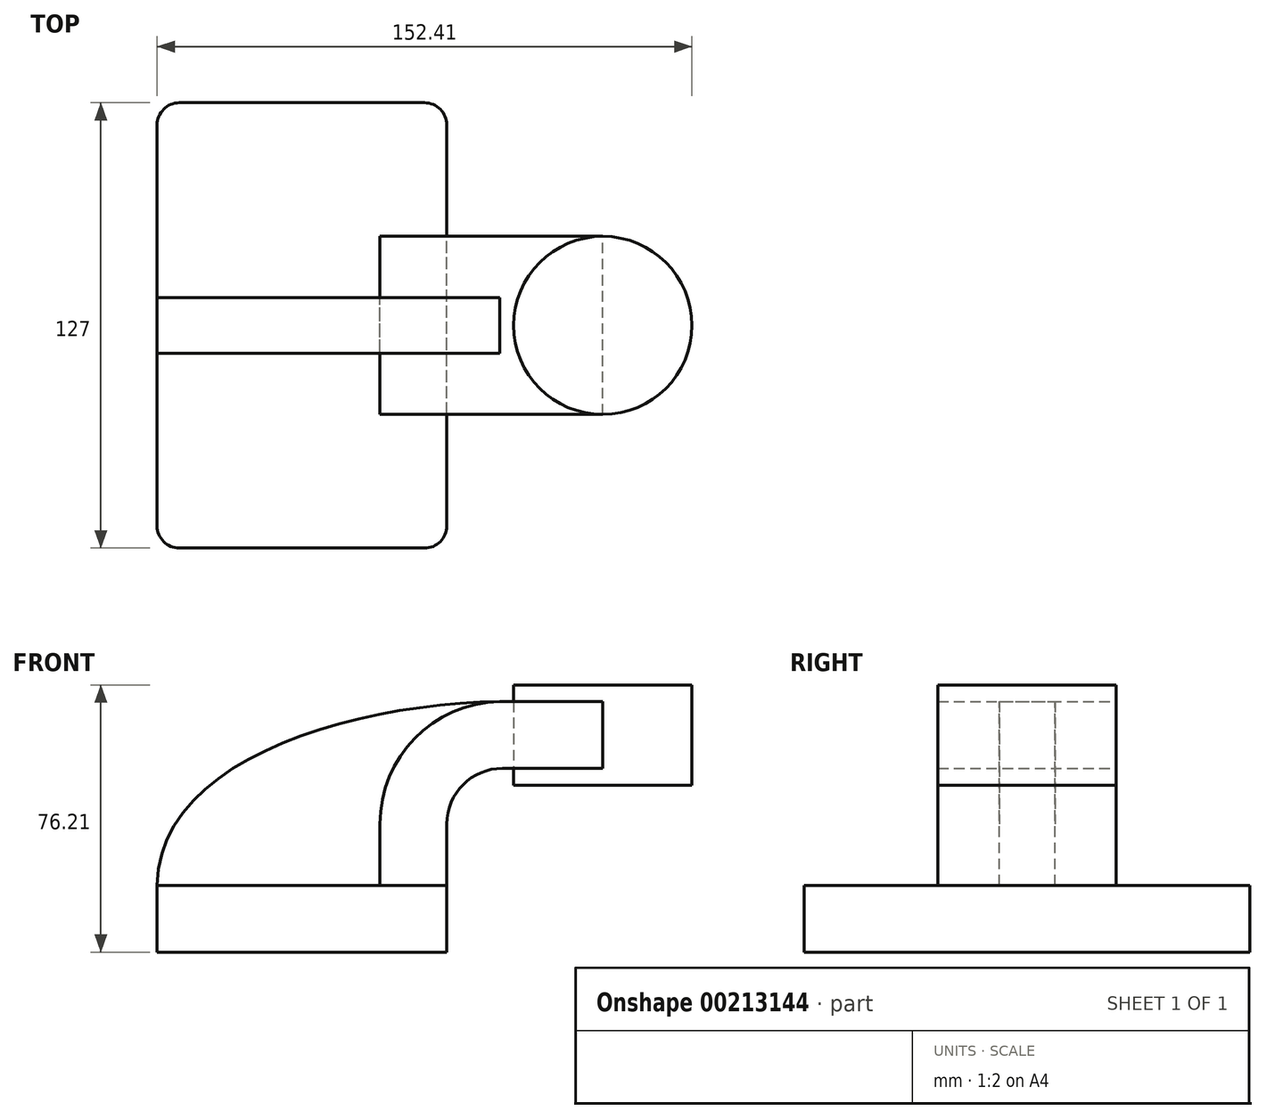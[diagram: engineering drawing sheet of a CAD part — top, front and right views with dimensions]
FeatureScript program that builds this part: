
annotation { "Feature Type Name" : "Feature", "Feature Type Description" : "" }
export const myFeature = defineFeature(function(context is Context, id is Id, definition is map)
    precondition{}
    {
        {
            var Q0;
            Q0=qCreatedBy(makeId("Front.planeOp"),FACE);
            var sketch = newSketch(context, id + "F0", { "sketchPlane" : qUnion([Q0])});
            skLineSegment(sketch, "E0.bottom", {"start": v(-41.28, 9.52) * mm, "end": v(41.28, 9.53) * mm});
            skLineSegment(sketch, "E0.top", {"start": v(-41.27, -9.52) * mm, "end": v(41.28, -9.52) * mm});
            skLineSegment(sketch, "E0.left", {"start": v(-41.28, 9.52) * mm, "end": v(-41.28, -9.53) * mm});
            skLineSegment(sketch, "E0.right", {"start": v(41.27, 9.53) * mm, "end": v(41.28, -9.52) * mm});
            skPoint(sketch, "E0.middle", {"position": v(0, 0) * mm});
            skLineSegment(sketch, "E1.bottom", {"start": v(111.12, 66.68) * mm, "end": v(60.32, 66.68) * mm});
            skLineSegment(sketch, "E1.top", {"start": v(111.12, 38.1) * mm, "end": v(60.32, 38.1) * mm});
            skLineSegment(sketch, "E1.left", {"start": v(111.12, 66.68) * mm, "end": v(111.12, 38.1) * mm});
            skLineSegment(sketch, "E1.right", {"start": v(60.32, 66.68) * mm, "end": v(60.32, 38.1) * mm});
            skPoint(sketch, "E1.middle", {"position": v(85.72, 52.39) * mm});
            skLineSegment(sketch, "E2", {"start": v(41.27, 9.53) * mm, "end": v(41.27, 27) * mm});
            skArc(sketch, "E3", {"start": v(41.27, 27) * mm, "mid": v(45.92, 38.23) * mm, "end": v(57.15, 42.88) * mm});
            skLineSegment(sketch, "E4", {"start": v(57.15, 42.88) * mm, "end": v(85.72, 42.88) * mm});
            skLineSegment(sketch, "E5.0", {"start": v(57.15, 61.93) * mm, "end": v(85.72, 61.93) * mm});
            skArc(sketch, "E5.1", {"start": v(22.22, 27) * mm, "mid": v(32.45, 51.7) * mm, "end": v(57.15, 61.93) * mm});
            skLineSegment(sketch, "E5.2", {"start": v(22.22, 9.53) * mm, "end": v(22.22, 27) * mm});
            skLineSegment(sketch, "E6", {"start": v(85.72, 38.1) * mm, "end": v(85.72, 66.68) * mm});
            skFitSpline(sketch, "E7", {"points": [v(-41.28, 9.52) * mm, v(57.15, 61.93) * mm], "startDerivative": vector(1.37, 108.93) * mm, "endDerivative": vector(126.16, 1.2) * mm});
            skSolve(sketch);
        }
        {
            var Q0;
            Q0=makeQuery(id+"F0.imprint","IMPRINT",FACE,{"disambiguationData":[TD([[makeQuery(id+"F0.imprint","IMPRINT",EDGE,{"derivedFrom":sQuery(id+"F0.wireOp",EDGE,"E0.top")}),1.0]])]});
            extrude(context, id + "F1", {"entities" : qUnion([Q0]), "endBound" : BoundingType.SYMMETRIC, "depth" : 127 * mm});
        }
        {
            var Q0;
            {var subQ1=sQuery(id+"F0.wireOp",EDGE,"E2");Q0=makeQuery(id+"F0.imprint","IMPRINT",FACE,{"disambiguationData":[TD([[makeQuery(id+"F0.imprint","IMPRINT",EDGE,{"derivedFrom":subQ1}),1.0]])]});}
            var Q1;
            {var subQ0=sQuery(id+"F0.wireOp",EDGE,"E5.0");var subQ1=sQuery(id+"F0.wireOp",EDGE,"E1.right");var subQ2=makeQuery(id+"F0.imprint","INTERSECT",VERTEX,{"derivedFrom":[subQ1,subQ0]});Q1=makeQuery(id+"F0.imprint","IMPRINT",FACE,{"disambiguationData":[TD([[makeQuery(id+"F0.imprint","IMPRINT",EDGE,{"disambiguationData":[TD([[subQ2,-1.0]])],"derivedFrom":subQ1}),1.0]])]});}
            extrude(context, id + "F2", {"entities" : qUnion([Q0, Q1]), "endBound" : BoundingType.SYMMETRIC, "depth" : 50.8 * mm});
        }
        {
            var Q0;
            {var subQ3=sQuery(id+"F0.wireOp",EDGE,"E5.2");Q0=makeQuery(id+"F0.imprint","IMPRINT",FACE,{"disambiguationData":[TD([[makeQuery(id+"F0.imprint","IMPRINT",EDGE,{"derivedFrom":subQ3}),1.0]])]});}
            extrude(context, id + "F3", {"entities" : qUnion([Q0]), "endBound" : BoundingType.SYMMETRIC, "depth" : 15.88 * mm});
        }
        {
            var Q0;
            {var subQ0=sQuery(id+"F0.wireOp",EDGE,"E1.left");Q0=makeQuery(id+"F0.imprint","IMPRINT",FACE,{"disambiguationData":[TD([[makeQuery(id+"F0.imprint","IMPRINT",EDGE,{"derivedFrom":subQ0}),-1.0]])]});}
            var Q1;
            Q1=sQuery(id+"F0.wireOp",EDGE,"E6");
            revolve(context, id + "F4", {"entities" : qUnion([Q0]), "axis" : qUnion([Q1]), "revolveType" : RevolveType.FULL});
        }
        {
            var Q0;
            Q0=makeQuery(id+"F1.opExtrude","CAP_EDGE",EDGE,{"disambiguationData":[OSD([sQuery(id+"F0.wireOp",EDGE,"E0.left")])],"isStart":false});
            var Q1;
            Q1=makeQuery(id+"F1.opExtrude","CAP_EDGE",EDGE,{"disambiguationData":[OSD([sQuery(id+"F0.wireOp",EDGE,"E0.right")])],"isStart":false});
            var Q2;
            Q2=makeQuery(id+"F1.opExtrude","CAP_EDGE",EDGE,{"disambiguationData":[OSD([sQuery(id+"F0.wireOp",EDGE,"E0.left")])],"isStart":true});
            var Q3;
            Q3=makeQuery(id+"F1.opExtrude","CAP_EDGE",EDGE,{"disambiguationData":[OSD([sQuery(id+"F0.wireOp",EDGE,"E0.right")])],"isStart":true});
            fillet(context, id + "F5", {"entities" : qUnion([Q0, Q1, Q2, Q3]), "radius" : 6.35 * mm, "tangentPropagation" : true, "allowEdgeOverflow" : false});
        }
    });
